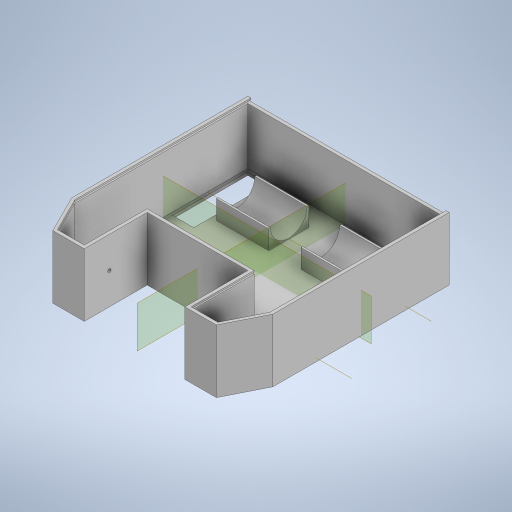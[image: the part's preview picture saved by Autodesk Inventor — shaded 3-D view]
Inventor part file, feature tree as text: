
AUTODESK INVENTOR PART (.ipt)
format: ipt  version: 2024 (Build 280153000, 153)  size: 560,640 bytes
history: native  units: in
note: dims shown in document units (in); Inventor stores cm internally (conversion verified against a paired STEP export)
features: projected_geometry x18, extrude x12, sketch x11, other x6, plane x4
ambient origin geometry x8: Origin, YZ Plane, XZ Plane, XY Plane, X Axis, Y Axis, Z Axis, Center Point
bodies: Solid1 (feature_tree)
feature tree (51):
  extrude  "Base"  Depth=3.0in
  extrude  "Wall"  TaperAngle=0.0deg  [1 undecoded]
  extrude  "Cuttout"  Depth=0.125in
  extrude  "Wheels"  Depth=0.125in
  plane  "Work Plane2"
  plane  "Work Plane3"
  extrude  "Extrusion11"  TaperAngle=0.0deg  [1 undecoded]
  sketch  "Sketch12"  dims[d50=1.0in d51=0.0in d52=0.125in]
  extrude  "Extrusion12"  Depth=0.125in
  extrude  "Extrusion13"  Depth=1.25in
  plane  "Work Plane4"
  extrude  "Extrusion14"  Depth=1.0in TaperAngle=0.0deg
  other  "Work Point1"
  other  "Work Point2"
  other  "Work Point3"
  other  "Work Point4"
  other  "Work Axis2"
  other  "Work Axis3"
  extrude  "Extrusion16"  Depth=1.0in TaperAngle=0.0deg
  plane  "Work Plane5"
  extrude  "Extrusion17"  Depth=1.0in
  extrude  "Extrusion18"  Depth=0.8in
  extrude  "Extrusion19"  TaperAngle=0.0deg  [1 undecoded]
  sketch  "Sketch1"  dims[d3=0.0in d8=3.0in]
  sketch  "Sketch2"  dims[d12=0.0in d13=0.0in d16=0.0in]
  sketch  "Sketch3"  dims[d21=0.275in d30=0.125in]
  projected_geometry  "Projected Loop1"
  sketch  "Sketch7"  dims[d31=0.125in d32=0.125in]
  projected_geometry  "Projected Loop3"
  sketch  "Sketch11"  dims[d33=0.125in d35=0.0in d36=0.0in]
  projected_geometry  "Projected Loop7"
  projected_geometry  "Projected Loop8"
  projected_geometry  "Projected Loop9"
  sketch  "Sketch13"  dims[d53=1.5in d54=1.25in]
  sketch  "Sketch15"  dims[d55=1.0in d56=0.0in d57=1.0in d58=0.0in]
  projected_geometry  "Projected Loop12"
  sketch  "Sketch17"  dims[d59=0.122in d60=1.0in d61=0.0in]
  projected_geometry  "Projected Loop14"
  projected_geometry  "Projected Loop15"
  projected_geometry  "Projected Loop16"
  projected_geometry  "Projected Loop17"
  projected_geometry  "Projected Loop18"
  projected_geometry  "Projected Loop19"
  projected_geometry  "Projected Loop20"
  projected_geometry  "Projected Loop21"
  projected_geometry  "Projected Loop22"
  projected_geometry  "Projected Loop24"
  sketch  "Sketch20"  dims[d72=-1.25in d74=1.0in]
  projected_geometry  "Projected Loop25"
  sketch  "Sketch22"  dims[d75=0.125in d76=2.875in d77=0.0in d82=0.0in d87=0.0625in d88=0.0625in d89=0.0625in d90=0.0in d92=0.2in d93=1.6in d95=2.08in d96=0.75in d97=0.0in d98=1.455in d99=5.5in d100=0.0in d101=0.8in]
  projected_geometry  "Projected Loop26"
note: 3 required parameter values undecoded (feature->parameter linkage not recoverable at this tier; creation-order binding heuristic only, values carry confidence <= 0.55)
